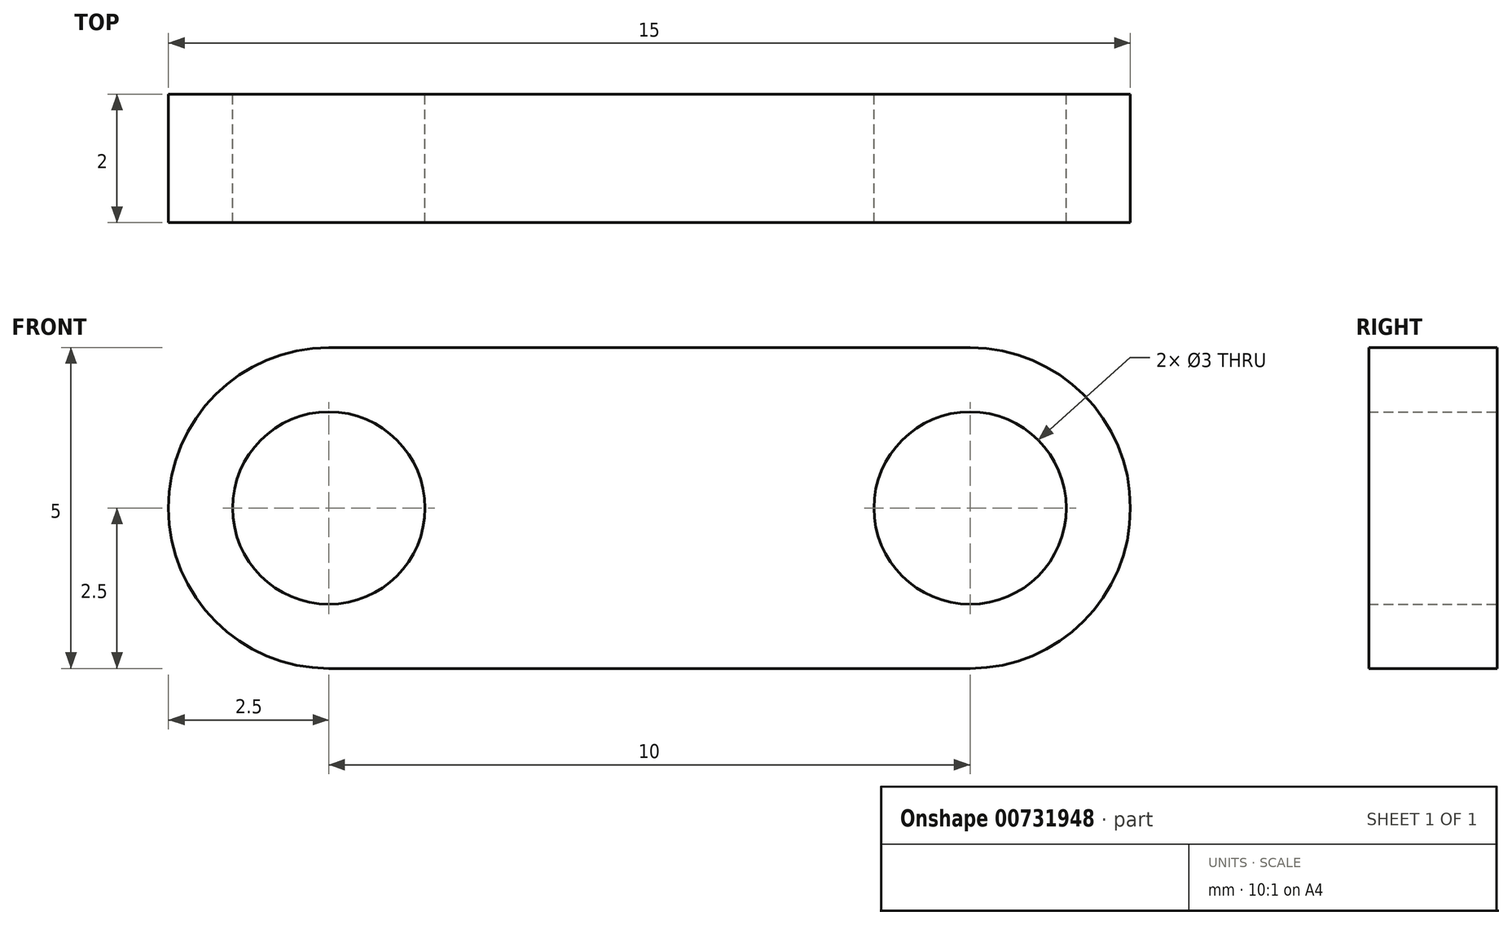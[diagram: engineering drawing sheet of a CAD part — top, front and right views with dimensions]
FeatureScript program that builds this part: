
annotation { "Feature Type Name" : "Feature", "Feature Type Description" : "" }
export const myFeature = defineFeature(function(context is Context, id is Id, definition is map)
    precondition{}
    {
        {
            var Q0;
            Q0=qCreatedBy(makeId("Front.planeOp"),FACE);
            var sketch = newSketch(context, id + "F0", { "sketchPlane" : qUnion([Q0])});
            skCircle(sketch, "E0", {"center": v(0, 0) * mm, "radius": 1.5 * mm});
            skLineSegment(sketch, "E1", {"start": v(0, 0) * mm, "end": v(10, 0) * mm, "construction": true});
            skCircle(sketch, "E2", {"center": v(10, 0) * mm, "radius": 1.5 * mm});
            skArc(sketch, "E3", {"start": v(0, 2.5) * mm, "mid": v(-2.5, 0) * mm, "end": v(0, -2.5) * mm});
            skArc(sketch, "E4", {"start": v(10, -2.5) * mm, "mid": v(12.5, 0) * mm, "end": v(10, 2.5) * mm});
            skLineSegment(sketch, "E5", {"start": v(0, 2.5) * mm, "end": v(10, 2.5) * mm});
            skLineSegment(sketch, "E6.MirrorCS", {"start": v(0, -2.5) * mm, "end": v(10, -2.5) * mm});
            skSolve(sketch);
        }
        {
            var Q0;
            Q0 = qSketchRegion(id + "F0", true);
            extrude(context, id + "F1", {"entities" : qUnion([Q0]), "depth" : 2 * mm, "offsetDistance" : 25.4 * mm});
        }
    });
